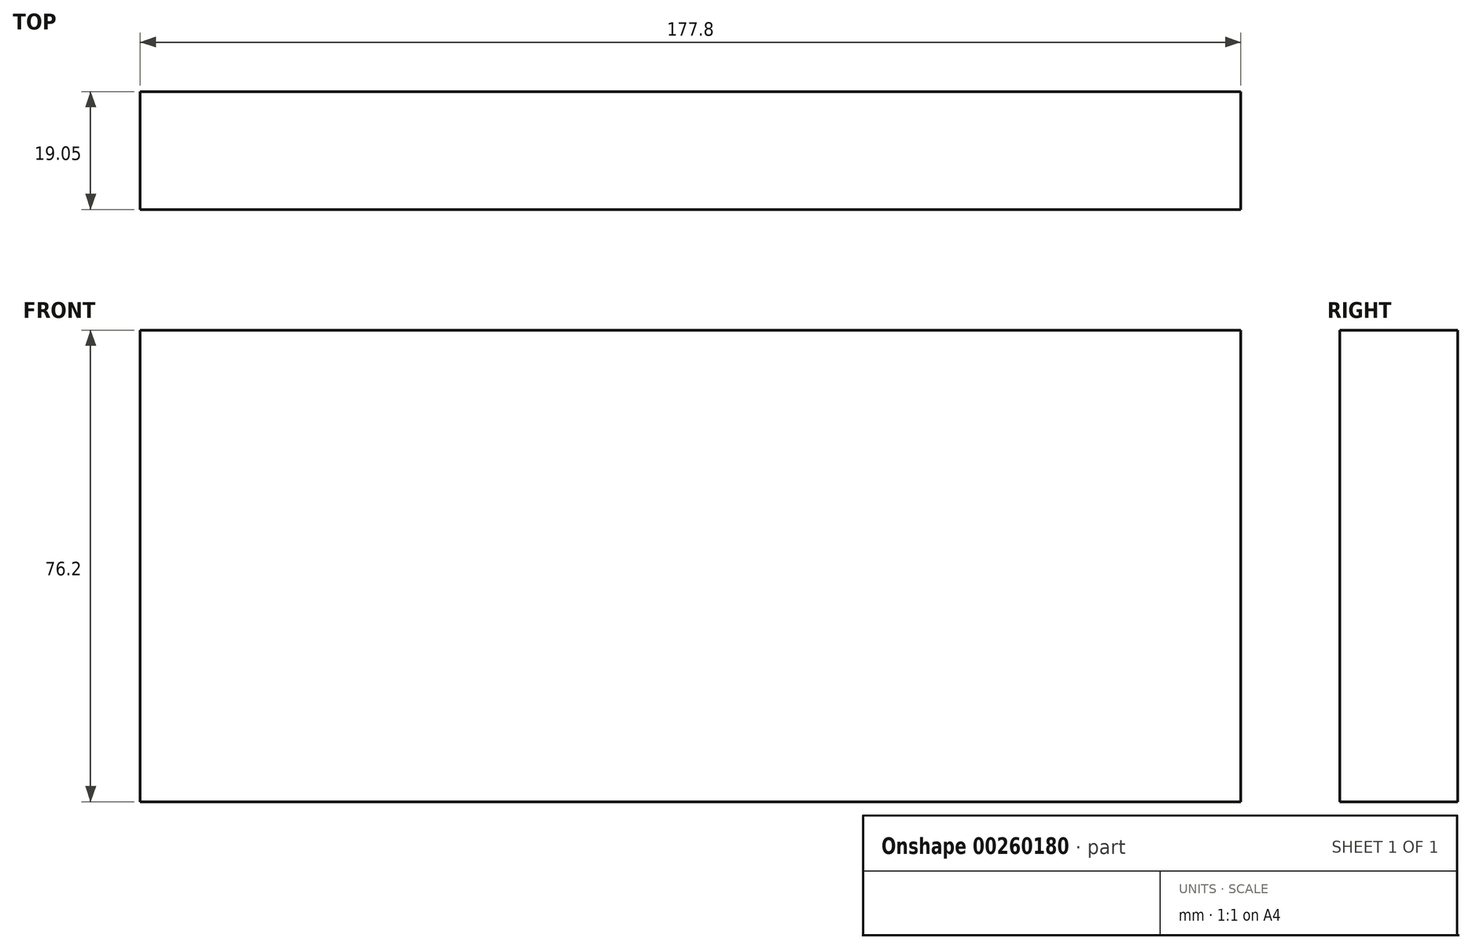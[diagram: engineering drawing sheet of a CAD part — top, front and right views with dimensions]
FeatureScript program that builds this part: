
annotation { "Feature Type Name" : "Feature", "Feature Type Description" : "" }
export const myFeature = defineFeature(function(context is Context, id is Id, definition is map)
    precondition{}
    {
        {
            var Q0;
            Q0=qCreatedBy(makeId("Front.planeOp"),FACE);
            var sketch = newSketch(context, id + "F0", { "sketchPlane" : qUnion([Q0])});
            skLineSegment(sketch, "E0.bottom", {"start": v(-41.4, 46.22) * mm, "end": v(136.4, 46.22) * mm});
            skLineSegment(sketch, "E0.top", {"start": v(-41.4, -29.98) * mm, "end": v(136.4, -29.98) * mm});
            skLineSegment(sketch, "E0.left", {"start": v(-41.4, 46.22) * mm, "end": v(-41.4, -29.98) * mm});
            skLineSegment(sketch, "E0.right", {"start": v(136.4, 46.22) * mm, "end": v(136.4, -29.98) * mm});
            skSolve(sketch);
        }
        {
            var Q0;
            Q0 = qSketchRegion(id + "F0", true);
            extrude(context, id + "F1", {"entities" : qUnion([Q0]), "depth" : 19.05 * mm});
        }
    });
